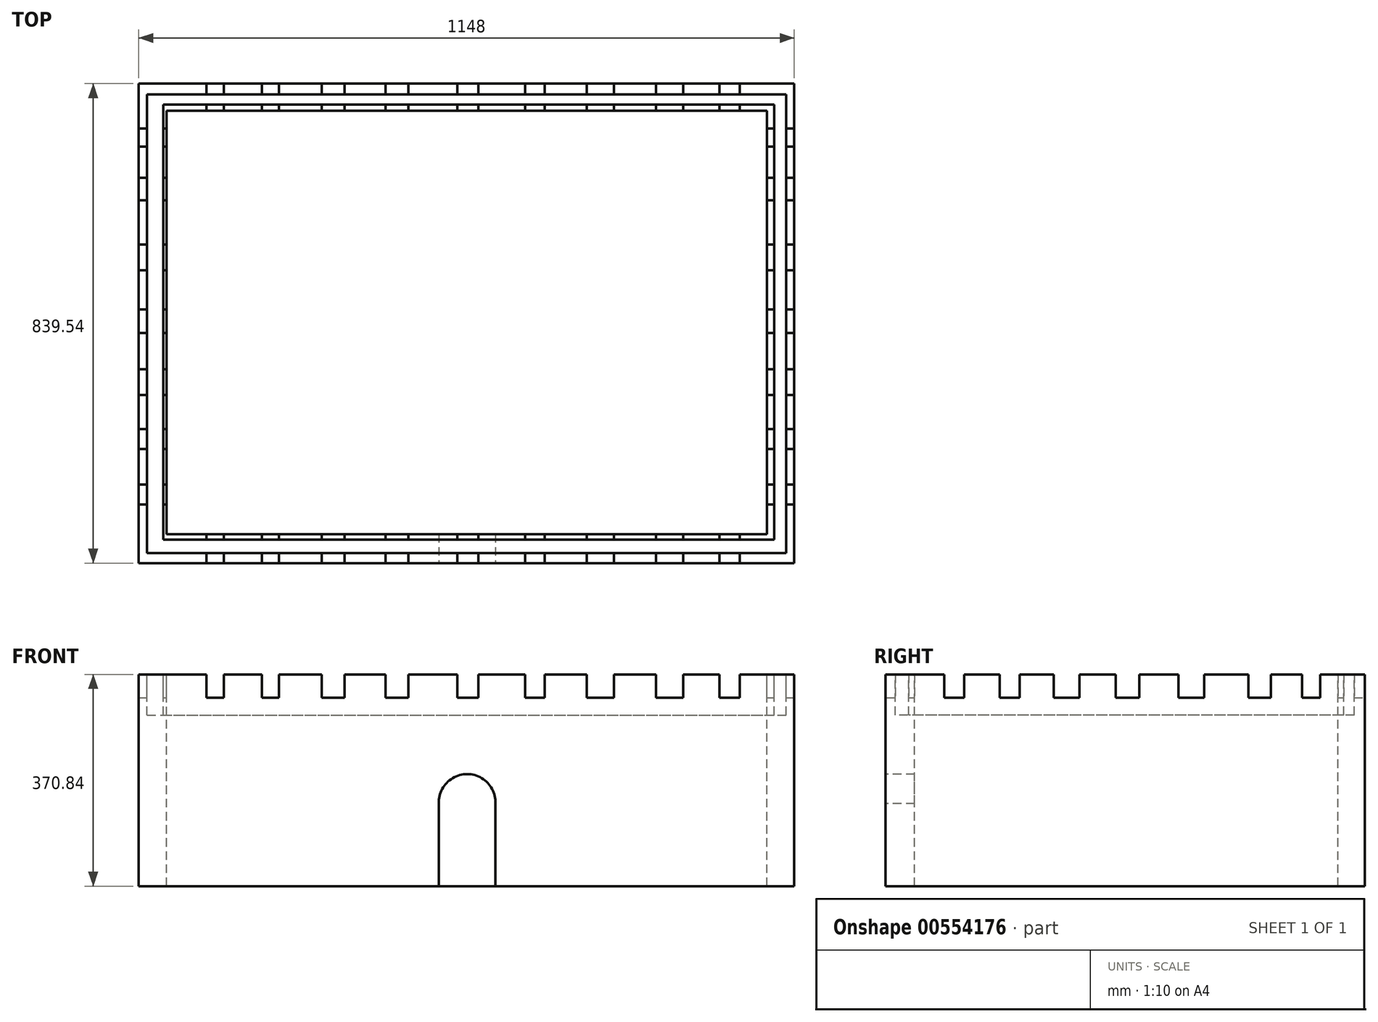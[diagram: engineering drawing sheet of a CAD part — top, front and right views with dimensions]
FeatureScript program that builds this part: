
annotation { "Feature Type Name" : "Feature", "Feature Type Description" : "" }
export const myFeature = defineFeature(function(context is Context, id is Id, definition is map)
    precondition{}
    {
        {
            var Q0;
            Q0=qCreatedBy(makeId("Top.planeOp"),FACE);
            var sketch = newSketch(context, id + "F0", { "sketchPlane" : qUnion([Q0])});
            skLineSegment(sketch, "E0.bottom", {"start": v(-575.13, 417.36) * mm, "end": v(572.87, 417.36) * mm});
            skLineSegment(sketch, "E0.top", {"start": v(-575.13, -422.18) * mm, "end": v(572.87, -422.18) * mm});
            skLineSegment(sketch, "E0.left", {"start": v(-575.13, 417.36) * mm, "end": v(-575.13, -422.18) * mm});
            skLineSegment(sketch, "E0.right", {"start": v(572.87, 417.36) * mm, "end": v(572.87, -422.18) * mm});
            skSolve(sketch);
        }
        {
            var Q0;
            Q0=makeQuery(id+"F0.imprint","IMPRINT",FACE,{"disambiguationData":[TD([[makeQuery(id+"F0.imprint","IMPRINT",EDGE,{"derivedFrom":sQuery(id+"F0.wireOp",EDGE,"E0.bottom")}),-1.0]])]});
            extrude(context, id + "F1", {"entities" : qUnion([Q0]), "depth" : 370.84 * mm, "offsetDistance" : 25.4 * mm});
        }
        {
            var Q0;
            Q0=makeQuery(id+"F1.opExtrude","CAP_FACE",FACE,{"disambiguationData":[OSD([sQuery(id+"F0.wireOp",EDGE,"E0.bottom"),sQuery(id+"F0.wireOp",EDGE,"E0.top"),sQuery(id+"F0.wireOp",EDGE,"E0.left"),sQuery(id+"F0.wireOp",EDGE,"E0.right")])],"isStart":false});
            var sketch = newSketch(context, id + "F2", { "sketchPlane" : qUnion([Q0])});
            skLineSegment(sketch, "E1.bottom", {"start": v(-523.99, 369.8) * mm, "end": v(524.91, 369.8) * mm});
            skLineSegment(sketch, "E1.top", {"start": v(-523.99, -369.85) * mm, "end": v(524.91, -369.85) * mm});
            skLineSegment(sketch, "E1.left", {"start": v(-523.99, 369.8) * mm, "end": v(-523.99, -369.85) * mm});
            skLineSegment(sketch, "E1.right", {"start": v(524.91, 369.8) * mm, "end": v(524.91, -369.85) * mm});
            skSolve(sketch);
        }
        {
            var Q0;
            Q0=makeQuery(id+"F1.opExtrude","CAP_FACE",FACE,{"disambiguationData":[OSD([sQuery(id+"F0.wireOp",EDGE,"E0.bottom"),sQuery(id+"F0.wireOp",EDGE,"E0.top"),sQuery(id+"F0.wireOp",EDGE,"E0.left"),sQuery(id+"F0.wireOp",EDGE,"E0.right")])],"isStart":false});
            var sketch = newSketch(context, id + "F3", { "sketchPlane" : qUnion([Q0])});
            skSolve(sketch);
        }
        {
            var Q0;
            Q0 = qSketchRegion(id + "F2", true);
            extrude(context, id + "F4", {"entities" : qUnion([Q0]), "operationType" : NewBodyOperationType.REMOVE, "oppositeDirection" : true, "depth" : 386.08 * mm, "offsetDistance" : 25.4 * mm});
        }
        {
            var Q0;
            Q0=makeQuery(id+"F3.imprint","IMPRINT",FACE,{"disambiguationData":[TD([[makeQuery(id+"F3.imprint","IMPRINT",EDGE,{"derivedFrom":makeQuery(id+"F1.opExtrude","CAP_EDGE",EDGE,{"disambiguationData":[OSD([sQuery(id+"F0.wireOp",EDGE,"E0.bottom")])],"isStart":false})}),-1.0]])]});
            var sketch = newSketch(context, id + "F5", { "sketchPlane" : qUnion([Q0])});
            skLineSegment(sketch, "E2.bottom", {"start": v(-560.65, 398.5) * mm, "end": v(558.39, 398.5) * mm});
            skLineSegment(sketch, "E2.top", {"start": v(-560.65, -404.92) * mm, "end": v(558.39, -404.92) * mm});
            skLineSegment(sketch, "E2.left", {"start": v(-560.65, 398.5) * mm, "end": v(-560.65, -404.92) * mm});
            skLineSegment(sketch, "E2.right", {"start": v(558.39, 398.5) * mm, "end": v(558.39, -404.92) * mm});
            skSolve(sketch);
        }
        {
            var Q0;
            Q0 = qSketchRegion(id + "F5", true);
            extrude(context, id + "F6", {"entities" : qUnion([Q0]), "operationType" : NewBodyOperationType.REMOVE, "oppositeDirection" : true, "depth" : 71.12 * mm, "offsetDistance" : 25.4 * mm});
        }
        {
            var Q0;
            Q0=makeQuery(id+"F3.imprint","IMPRINT",FACE,{"disambiguationData":[TD([[makeQuery(id+"F3.imprint","IMPRINT",EDGE,{"derivedFrom":makeQuery(id+"F1.opExtrude","CAP_EDGE",EDGE,{"disambiguationData":[OSD([sQuery(id+"F0.wireOp",EDGE,"E0.bottom")])],"isStart":false})}),-1.0]])]});
            var sketch = newSketch(context, id + "F7", { "sketchPlane" : qUnion([Q0])});
            skLineSegment(sketch, "E3.bottom", {"start": v(-532.12, 380.5) * mm, "end": v(537.5, 380.5) * mm});
            skLineSegment(sketch, "E3.top", {"start": v(-532.12, -381.47) * mm, "end": v(537.5, -381.47) * mm});
            skLineSegment(sketch, "E3.left", {"start": v(-532.12, 380.5) * mm, "end": v(-532.12, -381.47) * mm});
            skLineSegment(sketch, "E3.right", {"start": v(537.5, 380.5) * mm, "end": v(537.5, -381.47) * mm});
            skSolve(sketch);
        }
        {
            var Q0;
            Q0 = qSketchRegion(id + "F7", true);
            extrude(context, id + "F8", {"entities" : qUnion([Q0]), "operationType" : NewBodyOperationType.ADD, "oppositeDirection" : true, "depth" : 271.78 * mm, "offsetDistance" : 25.4 * mm});
        }
        {
            var Q0;
            Q0=makeQuery(id+"F3.imprint","IMPRINT",FACE,{"disambiguationData":[TD([[makeQuery(id+"F3.imprint","IMPRINT",EDGE,{"derivedFrom":makeQuery(id+"F1.opExtrude","CAP_EDGE",EDGE,{"disambiguationData":[OSD([sQuery(id+"F0.wireOp",EDGE,"E0.bottom")])],"isStart":false})}),-1.0]])]});
            var sketch = newSketch(context, id + "F9", { "sketchPlane" : qUnion([Q0])});
            skLineSegment(sketch, "E4.bottom", {"start": v(-526.8, 369.85) * mm, "end": v(524.91, 369.85) * mm});
            skLineSegment(sketch, "E4.top", {"start": v(-526.8, -371.46) * mm, "end": v(524.91, -371.46) * mm});
            skLineSegment(sketch, "E4.left", {"start": v(-526.8, 369.85) * mm, "end": v(-526.8, -371.46) * mm});
            skLineSegment(sketch, "E4.right", {"start": v(524.91, 369.85) * mm, "end": v(524.91, -371.46) * mm});
            skSolve(sketch);
        }
        {
            var Q0;
            Q0 = qSketchRegion(id + "F9", true);
            extrude(context, id + "F10", {"entities" : qUnion([Q0]), "operationType" : NewBodyOperationType.REMOVE, "oppositeDirection" : true, "depth" : 421.64 * mm, "offsetDistance" : 25.4 * mm});
        }
        {
            var Q0;
            Q0=makeQuery(id+"F3.imprint","IMPRINT",FACE,{"disambiguationData":[TD([[makeQuery(id+"F3.imprint","IMPRINT",EDGE,{"derivedFrom":makeQuery(id+"F1.opExtrude","CAP_EDGE",EDGE,{"disambiguationData":[OSD([sQuery(id+"F0.wireOp",EDGE,"E0.bottom")])],"isStart":false})}),-1.0]])]});
            var sketch = newSketch(context, id + "F11", { "sketchPlane" : qUnion([Q0])});
            skLineSegment(sketch, "E5.bottom", {"start": v(-611.66, 22.3) * mm, "end": v(642.87, 22.3) * mm});
            skLineSegment(sketch, "E5.top", {"start": v(-611.66, -19.15) * mm, "end": v(642.87, -19.15) * mm});
            skLineSegment(sketch, "E5.left", {"start": v(-611.66, 22.3) * mm, "end": v(-611.66, -19.15) * mm});
            skLineSegment(sketch, "E5.right", {"start": v(642.87, 22.3) * mm, "end": v(642.87, -19.15) * mm});
            skLineSegment(sketch, "E6.bottom", {"start": v(153.5, 22.3) * mm, "end": v(153.5, 22.3) * mm});
            skLineSegment(sketch, "E6.top", {"start": v(153.5, -19.15) * mm, "end": v(153.5, -19.15) * mm});
            skLineSegment(sketch, "E6.left", {"start": v(153.5, 22.3) * mm, "end": v(153.5, -19.15) * mm});
            skLineSegment(sketch, "E6.right", {"start": v(153.5, 22.3) * mm, "end": v(153.5, -19.15) * mm});
            skSolve(sketch);
        }
        {
            var Q0;
            Q0 = qSketchRegion(id + "F11", true);
            extrude(context, id + "F12", {"entities" : qUnion([Q0]), "operationType" : NewBodyOperationType.REMOVE, "oppositeDirection" : true, "depth" : 40.64 * mm, "offsetDistance" : 25.4 * mm});
        }
        {
            var Q0;
            Q0=makeQuery(id+"F3.imprint","IMPRINT",FACE,{"disambiguationData":[TD([[makeQuery(id+"F3.imprint","IMPRINT",EDGE,{"derivedFrom":makeQuery(id+"F1.opExtrude","CAP_EDGE",EDGE,{"disambiguationData":[OSD([sQuery(id+"F0.wireOp",EDGE,"E0.bottom")])],"isStart":false})}),-1.0]])]});
            var sketch = newSketch(context, id + "F13", { "sketchPlane" : qUnion([Q0])});
            skLineSegment(sketch, "E7.bottom", {"start": v(-17.07, -430.42) * mm, "end": v(19.6, -430.42) * mm});
            skLineSegment(sketch, "E7.top", {"start": v(-17.07, 436.75) * mm, "end": v(19.6, 436.75) * mm});
            skLineSegment(sketch, "E7.left", {"start": v(-17.07, -430.42) * mm, "end": v(-17.07, 436.75) * mm});
            skLineSegment(sketch, "E7.right", {"start": v(19.6, -430.42) * mm, "end": v(19.6, 436.75) * mm});
            skSolve(sketch);
        }
        {
            var Q0;
            {var subQ0=sQuery(id+"F13.wireOp",EDGE,"E7.left");var subQ1=makeQuery(id+"F3.imprint","IMPRINT",EDGE,{"derivedFrom":makeQuery(id+"F1.opExtrude","CAP_EDGE",EDGE,{"disambiguationData":[OSD([sQuery(id+"F0.wireOp",EDGE,"E0.top")])],"isStart":false})});var subQ2=makeQuery(id+"F13.imprint","INTERSECT",VERTEX,{"derivedFrom":[subQ1,subQ0]});Q0=makeQuery(id+"F13.imprint","IMPRINT",FACE,{"disambiguationData":[TD([[makeQuery(id+"F13.imprint","IMPRINT",EDGE,{"disambiguationData":[TD([[subQ2,-1.0]])],"derivedFrom":subQ0}),-1.0]])]});}
            extrude(context, id + "F14", {"entities" : qUnion([Q0]), "operationType" : NewBodyOperationType.REMOVE, "oppositeDirection" : true, "depth" : 40.64 * mm, "offsetDistance" : 25.4 * mm});
        }
        {
            var Q0;
            Q0=makeQuery(id+"F3.imprint","IMPRINT",FACE,{"disambiguationData":[TD([[makeQuery(id+"F3.imprint","IMPRINT",EDGE,{"derivedFrom":makeQuery(id+"F1.opExtrude","CAP_EDGE",EDGE,{"disambiguationData":[OSD([sQuery(id+"F0.wireOp",EDGE,"E0.bottom")])],"isStart":false})}),-1.0]])]});
            var sketch = newSketch(context, id + "F15", { "sketchPlane" : qUnion([Q0])});
            skLineSegment(sketch, "E8.bottom", {"start": v(-103.15, 424) * mm, "end": v(-143, 424) * mm});
            skLineSegment(sketch, "E8.top", {"start": v(-103.15, -433.6) * mm, "end": v(-143, -433.6) * mm});
            skLineSegment(sketch, "E8.left", {"start": v(-103.15, 424) * mm, "end": v(-103.15, -433.6) * mm});
            skLineSegment(sketch, "E8.right", {"start": v(-143, 424) * mm, "end": v(-143, -433.6) * mm});
            skSolve(sketch);
        }
        {
            var Q0;
            Q0 = qSketchRegion(id + "F15", true);
            extrude(context, id + "F16", {"entities" : qUnion([Q0]), "operationType" : NewBodyOperationType.REMOVE, "oppositeDirection" : true, "depth" : 40.64 * mm, "offsetDistance" : 25.4 * mm});
        }
        {
            var Q0;
            Q0=makeQuery(id+"F3.imprint","IMPRINT",FACE,{"disambiguationData":[TD([[makeQuery(id+"F3.imprint","IMPRINT",EDGE,{"derivedFrom":makeQuery(id+"F1.opExtrude","CAP_EDGE",EDGE,{"disambiguationData":[OSD([sQuery(id+"F0.wireOp",EDGE,"E0.bottom")])],"isStart":false})}),-1.0]])]});
            var sketch = newSketch(context, id + "F17", { "sketchPlane" : qUnion([Q0])});
            skLineSegment(sketch, "E9.bottom", {"start": v(101.33, 424.13) * mm, "end": v(135.45, 424.13) * mm});
            skLineSegment(sketch, "E9.top", {"start": v(101.33, -425.13) * mm, "end": v(135.45, -425.13) * mm});
            skLineSegment(sketch, "E9.left", {"start": v(101.33, 424.13) * mm, "end": v(101.33, -425.13) * mm});
            skLineSegment(sketch, "E9.right", {"start": v(135.45, 424.13) * mm, "end": v(135.45, -425.13) * mm});
            skSolve(sketch);
        }
        {
            var Q0;
            Q0 = qSketchRegion(id + "F17", true);
            extrude(context, id + "F18", {"entities" : qUnion([Q0]), "operationType" : NewBodyOperationType.REMOVE, "oppositeDirection" : true, "depth" : 40.64 * mm, "offsetDistance" : 25.4 * mm});
        }
        {
            var Q0;
            Q0=makeQuery(id+"F3.imprint","IMPRINT",FACE,{"disambiguationData":[TD([[makeQuery(id+"F3.imprint","IMPRINT",EDGE,{"derivedFrom":makeQuery(id+"F1.opExtrude","CAP_EDGE",EDGE,{"disambiguationData":[OSD([sQuery(id+"F0.wireOp",EDGE,"E0.bottom")])],"isStart":false})}),-1.0]])]});
            var sketch = newSketch(context, id + "F19", { "sketchPlane" : qUnion([Q0])});
            skLineSegment(sketch, "E10.bottom", {"start": v(-214.74, 427.19) * mm, "end": v(-254.59, 427.19) * mm});
            skLineSegment(sketch, "E10.top", {"start": v(-214.74, -433.6) * mm, "end": v(-254.59, -433.6) * mm});
            skLineSegment(sketch, "E10.left", {"start": v(-214.74, 427.19) * mm, "end": v(-214.74, -433.6) * mm});
            skLineSegment(sketch, "E10.right", {"start": v(-254.59, 427.19) * mm, "end": v(-254.59, -433.6) * mm});
            skSolve(sketch);
        }
        {
            var Q0;
            Q0 = qSketchRegion(id + "F19", true);
            extrude(context, id + "F20", {"entities" : qUnion([Q0]), "operationType" : NewBodyOperationType.REMOVE, "oppositeDirection" : true, "depth" : 40.64 * mm, "offsetDistance" : 25.4 * mm});
        }
        {
            var Q0;
            Q0=makeQuery(id+"F3.imprint","IMPRINT",FACE,{"disambiguationData":[TD([[makeQuery(id+"F3.imprint","IMPRINT",EDGE,{"derivedFrom":makeQuery(id+"F1.opExtrude","CAP_EDGE",EDGE,{"disambiguationData":[OSD([sQuery(id+"F0.wireOp",EDGE,"E0.bottom")])],"isStart":false})}),-1.0]])]});
            var sketch = newSketch(context, id + "F21", { "sketchPlane" : qUnion([Q0])});
            skLineSegment(sketch, "E11.bottom", {"start": v(-329.55, 425.56) * mm, "end": v(-359.86, 425.56) * mm});
            skLineSegment(sketch, "E11.top", {"start": v(-329.55, -459.36) * mm, "end": v(-359.86, -459.36) * mm});
            skLineSegment(sketch, "E11.left", {"start": v(-329.55, 425.56) * mm, "end": v(-329.55, -459.36) * mm});
            skLineSegment(sketch, "E11.right", {"start": v(-359.86, 425.56) * mm, "end": v(-359.86, -459.36) * mm});
            skSolve(sketch);
        }
        {
            var Q0;
            Q0 = qSketchRegion(id + "F21", true);
            extrude(context, id + "F22", {"entities" : qUnion([Q0]), "operationType" : NewBodyOperationType.REMOVE, "oppositeDirection" : true, "depth" : 40.64 * mm, "offsetDistance" : 25.4 * mm});
        }
        {
            var Q0;
            Q0=makeQuery(id+"F3.imprint","IMPRINT",FACE,{"disambiguationData":[TD([[makeQuery(id+"F3.imprint","IMPRINT",EDGE,{"derivedFrom":makeQuery(id+"F1.opExtrude","CAP_EDGE",EDGE,{"disambiguationData":[OSD([sQuery(id+"F0.wireOp",EDGE,"E0.bottom")])],"isStart":false})}),-1.0]])]});
            var sketch = newSketch(context, id + "F23", { "sketchPlane" : qUnion([Q0])});
            skLineSegment(sketch, "E12.bottom", {"start": v(-426.3, 422.82) * mm, "end": v(-456.6, 422.82) * mm});
            skLineSegment(sketch, "E12.top", {"start": v(-426.3, -426.82) * mm, "end": v(-456.6, -426.82) * mm});
            skLineSegment(sketch, "E12.left", {"start": v(-426.3, 422.82) * mm, "end": v(-426.3, -426.82) * mm});
            skLineSegment(sketch, "E12.right", {"start": v(-456.6, 422.82) * mm, "end": v(-456.6, -426.82) * mm});
            skSolve(sketch);
        }
        {
            var Q0;
            Q0 = qSketchRegion(id + "F23", true);
            extrude(context, id + "F24", {"entities" : qUnion([Q0]), "operationType" : NewBodyOperationType.REMOVE, "oppositeDirection" : true, "depth" : 40.64 * mm, "offsetDistance" : 25.4 * mm});
        }
        {
            var Q0;
            Q0=makeQuery(id+"F3.imprint","IMPRINT",FACE,{"disambiguationData":[TD([[makeQuery(id+"F3.imprint","IMPRINT",EDGE,{"derivedFrom":makeQuery(id+"F1.opExtrude","CAP_EDGE",EDGE,{"disambiguationData":[OSD([sQuery(id+"F0.wireOp",EDGE,"E0.bottom")])],"isStart":false})}),-1.0]])]});
            var sketch = newSketch(context, id + "F25", { "sketchPlane" : qUnion([Q0])});
            skLineSegment(sketch, "E13.bottom", {"start": v(209.29, 427.19) * mm, "end": v(257.1, 427.19) * mm});
            skLineSegment(sketch, "E13.top", {"start": v(209.29, -432.01) * mm, "end": v(257.1, -432.01) * mm});
            skLineSegment(sketch, "E13.left", {"start": v(209.29, 427.19) * mm, "end": v(209.29, -432.01) * mm});
            skLineSegment(sketch, "E13.right", {"start": v(257.1, 427.19) * mm, "end": v(257.1, -432.01) * mm});
            skSolve(sketch);
        }
        {
            var Q0;
            Q0 = qSketchRegion(id + "F25", true);
            extrude(context, id + "F26", {"entities" : qUnion([Q0]), "operationType" : NewBodyOperationType.REMOVE, "oppositeDirection" : true, "depth" : 40.64 * mm, "offsetDistance" : 25.4 * mm});
        }
        {
            var Q0;
            Q0=makeQuery(id+"F3.imprint","IMPRINT",FACE,{"disambiguationData":[TD([[makeQuery(id+"F3.imprint","IMPRINT",EDGE,{"derivedFrom":makeQuery(id+"F1.opExtrude","CAP_EDGE",EDGE,{"disambiguationData":[OSD([sQuery(id+"F0.wireOp",EDGE,"E0.bottom")])],"isStart":false})}),-1.0]])]});
            var sketch = newSketch(context, id + "F27", { "sketchPlane" : qUnion([Q0])});
            skLineSegment(sketch, "E14.bottom", {"start": v(330.44, 422.4) * mm, "end": v(378.26, 422.4) * mm});
            skLineSegment(sketch, "E14.top", {"start": v(330.44, -436.8) * mm, "end": v(378.26, -436.8) * mm});
            skLineSegment(sketch, "E14.left", {"start": v(330.44, 422.4) * mm, "end": v(330.44, -436.8) * mm});
            skLineSegment(sketch, "E14.right", {"start": v(378.26, 422.4) * mm, "end": v(378.26, -436.8) * mm});
            skSolve(sketch);
        }
        {
            var Q0;
            Q0 = qSketchRegion(id + "F27", true);
            extrude(context, id + "F28", {"entities" : qUnion([Q0]), "operationType" : NewBodyOperationType.REMOVE, "oppositeDirection" : true, "depth" : 40.64 * mm, "offsetDistance" : 25.4 * mm});
        }
        {
            var Q0;
            Q0=makeQuery(id+"F3.imprint","IMPRINT",FACE,{"disambiguationData":[TD([[makeQuery(id+"F3.imprint","IMPRINT",EDGE,{"derivedFrom":makeQuery(id+"F1.opExtrude","CAP_EDGE",EDGE,{"disambiguationData":[OSD([sQuery(id+"F0.wireOp",EDGE,"E0.bottom")])],"isStart":false})}),-1.0]])]});
            var sketch = newSketch(context, id + "F29", { "sketchPlane" : qUnion([Q0])});
            skLineSegment(sketch, "E15.bottom", {"start": v(442.02, 427.19) * mm, "end": v(477.1, 427.19) * mm});
            skLineSegment(sketch, "E15.top", {"start": v(442.02, -438.4) * mm, "end": v(477.1, -438.4) * mm});
            skLineSegment(sketch, "E15.left", {"start": v(442.02, 427.19) * mm, "end": v(442.02, -438.4) * mm});
            skLineSegment(sketch, "E15.right", {"start": v(477.1, 427.19) * mm, "end": v(477.1, -438.4) * mm});
            skSolve(sketch);
        }
        {
            var Q0;
            Q0 = qSketchRegion(id + "F29", true);
            extrude(context, id + "F30", {"entities" : qUnion([Q0]), "operationType" : NewBodyOperationType.REMOVE, "oppositeDirection" : true, "depth" : 40.64 * mm, "offsetDistance" : 25.4 * mm});
        }
        {
            var Q0;
            Q0=makeQuery(id+"F3.imprint","IMPRINT",FACE,{"disambiguationData":[TD([[makeQuery(id+"F3.imprint","IMPRINT",EDGE,{"derivedFrom":makeQuery(id+"F1.opExtrude","CAP_EDGE",EDGE,{"disambiguationData":[OSD([sQuery(id+"F0.wireOp",EDGE,"E0.bottom")])],"isStart":false})}),-1.0]])]});
            var sketch = newSketch(context, id + "F31", { "sketchPlane" : qUnion([Q0])});
            skLineSegment(sketch, "E16.bottom", {"start": v(-587.75, 90.84) * mm, "end": v(598.24, 90.84) * mm});
            skLineSegment(sketch, "E16.top", {"start": v(-587.75, 135.47) * mm, "end": v(598.24, 135.47) * mm});
            skLineSegment(sketch, "E16.left", {"start": v(-587.75, 90.84) * mm, "end": v(-587.75, 135.47) * mm});
            skLineSegment(sketch, "E16.right", {"start": v(598.24, 90.84) * mm, "end": v(598.24, 135.47) * mm});
            skSolve(sketch);
        }
        {
            var Q0;
            Q0 = qSketchRegion(id + "F31", true);
            extrude(context, id + "F32", {"entities" : qUnion([Q0]), "operationType" : NewBodyOperationType.REMOVE, "oppositeDirection" : true, "depth" : 40.64 * mm, "offsetDistance" : 25.4 * mm});
        }
        {
            var Q0;
            Q0=makeQuery(id+"F3.imprint","IMPRINT",FACE,{"disambiguationData":[TD([[makeQuery(id+"F3.imprint","IMPRINT",EDGE,{"derivedFrom":makeQuery(id+"F1.opExtrude","CAP_EDGE",EDGE,{"disambiguationData":[OSD([sQuery(id+"F0.wireOp",EDGE,"E0.bottom")])],"isStart":false})}),-1.0]])]});
            var sketch = newSketch(context, id + "F33", { "sketchPlane" : qUnion([Q0])});
            skLineSegment(sketch, "E17.bottom", {"start": v(-584.56, -82.91) * mm, "end": v(591.86, -82.91) * mm});
            skLineSegment(sketch, "E17.top", {"start": v(-584.56, -127.55) * mm, "end": v(591.86, -127.55) * mm});
            skLineSegment(sketch, "E17.left", {"start": v(-584.56, -82.91) * mm, "end": v(-584.56, -127.55) * mm});
            skLineSegment(sketch, "E17.right", {"start": v(591.86, -82.91) * mm, "end": v(591.86, -127.55) * mm});
            skSolve(sketch);
        }
        {
            var Q0;
            Q0 = qSketchRegion(id + "F33", true);
            extrude(context, id + "F34", {"entities" : qUnion([Q0]), "operationType" : NewBodyOperationType.REMOVE, "oppositeDirection" : true, "depth" : 40.64 * mm, "offsetDistance" : 25.4 * mm});
        }
        {
            var Q0;
            Q0=makeQuery(id+"F3.imprint","IMPRINT",FACE,{"disambiguationData":[TD([[makeQuery(id+"F3.imprint","IMPRINT",EDGE,{"derivedFrom":makeQuery(id+"F1.opExtrude","CAP_EDGE",EDGE,{"disambiguationData":[OSD([sQuery(id+"F0.wireOp",EDGE,"E0.bottom")])],"isStart":false})}),-1.0]])]});
            var sketch = newSketch(context, id + "F35", { "sketchPlane" : qUnion([Q0])});
            skLineSegment(sketch, "E18.bottom", {"start": v(591.66, 213) * mm, "end": v(-608.3, 213) * mm});
            skLineSegment(sketch, "E18.top", {"start": v(591.66, 252.8) * mm, "end": v(-608.3, 252.8) * mm});
            skLineSegment(sketch, "E18.left", {"start": v(591.66, 213) * mm, "end": v(591.66, 252.8) * mm});
            skLineSegment(sketch, "E18.right", {"start": v(-608.3, 213) * mm, "end": v(-608.3, 252.8) * mm});
            skSolve(sketch);
        }
        {
            var Q0;
            Q0 = qSketchRegion(id + "F35", true);
            extrude(context, id + "F36", {"entities" : qUnion([Q0]), "operationType" : NewBodyOperationType.REMOVE, "oppositeDirection" : true, "depth" : 40.64 * mm, "offsetDistance" : 25.4 * mm});
        }
        {
            var Q0;
            Q0=makeQuery(id+"F3.imprint","IMPRINT",FACE,{"disambiguationData":[TD([[makeQuery(id+"F3.imprint","IMPRINT",EDGE,{"derivedFrom":makeQuery(id+"F1.opExtrude","CAP_EDGE",EDGE,{"disambiguationData":[OSD([sQuery(id+"F0.wireOp",EDGE,"E0.bottom")])],"isStart":false})}),-1.0]])]});
            var sketch = newSketch(context, id + "F37", { "sketchPlane" : qUnion([Q0])});
            skLineSegment(sketch, "E19.bottom", {"start": v(587, 306.96) * mm, "end": v(-610.15, 306.96) * mm});
            skLineSegment(sketch, "E19.top", {"start": v(587, 338.84) * mm, "end": v(-610.15, 338.84) * mm});
            skLineSegment(sketch, "E19.left", {"start": v(587, 306.96) * mm, "end": v(587, 338.84) * mm});
            skLineSegment(sketch, "E19.right", {"start": v(-610.15, 306.96) * mm, "end": v(-610.15, 338.84) * mm});
            skSolve(sketch);
        }
        {
            var Q0;
            Q0 = qSketchRegion(id + "F37", true);
            extrude(context, id + "F38", {"entities" : qUnion([Q0]), "operationType" : NewBodyOperationType.REMOVE, "oppositeDirection" : true, "depth" : 40.64 * mm, "offsetDistance" : 25.4 * mm});
        }
        {
            var Q0;
            Q0=makeQuery(id+"F3.imprint","IMPRINT",FACE,{"disambiguationData":[TD([[makeQuery(id+"F3.imprint","IMPRINT",EDGE,{"derivedFrom":makeQuery(id+"F1.opExtrude","CAP_EDGE",EDGE,{"disambiguationData":[OSD([sQuery(id+"F0.wireOp",EDGE,"E0.bottom")])],"isStart":false})}),-1.0]])]});
            var sketch = newSketch(context, id + "F39", { "sketchPlane" : qUnion([Q0])});
            skLineSegment(sketch, "E20.bottom", {"start": v(-581.93, -187.69) * mm, "end": v(588.28, -187.69) * mm});
            skLineSegment(sketch, "E20.top", {"start": v(-581.93, -222.54) * mm, "end": v(588.28, -222.54) * mm});
            skLineSegment(sketch, "E20.left", {"start": v(-581.93, -187.69) * mm, "end": v(-581.93, -222.54) * mm});
            skLineSegment(sketch, "E20.right", {"start": v(588.28, -187.69) * mm, "end": v(588.28, -222.54) * mm});
            skSolve(sketch);
        }
        {
            var Q0;
            Q0 = qSketchRegion(id + "F39", true);
            extrude(context, id + "F40", {"entities" : qUnion([Q0]), "operationType" : NewBodyOperationType.REMOVE, "oppositeDirection" : true, "depth" : 40.64 * mm, "offsetDistance" : 25.4 * mm});
        }
        {
            var Q0;
            Q0=makeQuery(id+"F3.imprint","IMPRINT",FACE,{"disambiguationData":[TD([[makeQuery(id+"F3.imprint","IMPRINT",EDGE,{"derivedFrom":makeQuery(id+"F1.opExtrude","CAP_EDGE",EDGE,{"disambiguationData":[OSD([sQuery(id+"F0.wireOp",EDGE,"E0.bottom")])],"isStart":false})}),-1.0]])]});
            var sketch = newSketch(context, id + "F41", { "sketchPlane" : qUnion([Q0])});
            skLineSegment(sketch, "E21.bottom", {"start": v(-587.4, -284.86) * mm, "end": v(585.5, -284.86) * mm});
            skLineSegment(sketch, "E21.top", {"start": v(-587.4, -319.7) * mm, "end": v(585.5, -319.7) * mm});
            skLineSegment(sketch, "E21.left", {"start": v(-587.4, -284.86) * mm, "end": v(-587.4, -319.7) * mm});
            skLineSegment(sketch, "E21.right", {"start": v(585.5, -284.86) * mm, "end": v(585.5, -319.7) * mm});
            skSolve(sketch);
        }
        {
            var Q0;
            Q0 = qSketchRegion(id + "F41", true);
            extrude(context, id + "F42", {"entities" : qUnion([Q0]), "operationType" : NewBodyOperationType.REMOVE, "oppositeDirection" : true, "depth" : 40.64 * mm, "offsetDistance" : 25.4 * mm});
        }
        {
            var Q0;
            Q0=makeQuery(id+"F1.opExtrude","SWEPT_FACE",FACE,{"disambiguationData":[OSD([sQuery(id+"F0.wireOp",EDGE,"E0.top")])]});
            var sketch = newSketch(context, id + "F43", { "sketchPlane" : qUnion([Q0])});
            skCircle(sketch, "E22", {"center": v(0, 146.45) * mm, "radius": 49.69 * mm});
            skSolve(sketch);
        }
        {
            var Q0;
            Q0 = qSketchRegion(id + "F43", true);
            extrude(context, id + "F44", {"entities" : qUnion([Q0]), "operationType" : NewBodyOperationType.REMOVE, "oppositeDirection" : true, "depth" : 93.98 * mm, "offsetDistance" : 25.4 * mm});
        }
        {
            var Q0;
            Q0=makeQuery(id+"F1.opExtrude","SWEPT_FACE",FACE,{"disambiguationData":[OSD([sQuery(id+"F0.wireOp",EDGE,"E0.top")])]});
            var sketch = newSketch(context, id + "F45", { "sketchPlane" : qUnion([Q0])});
            skLineSegment(sketch, "E23.bottom", {"start": v(-49.97, 0) * mm, "end": v(49.65, 0) * mm});
            skLineSegment(sketch, "E23.top", {"start": v(-49.97, 144.43) * mm, "end": v(49.65, 144.43) * mm});
            skLineSegment(sketch, "E23.left", {"start": v(-49.97, 0) * mm, "end": v(-49.97, 144.43) * mm});
            skLineSegment(sketch, "E23.right", {"start": v(49.65, 0) * mm, "end": v(49.65, 144.43) * mm});
            skSolve(sketch);
        }
        {
            var Q0;
            Q0 = qSketchRegion(id + "F45", true);
            extrude(context, id + "F46", {"entities" : qUnion([Q0]), "operationType" : NewBodyOperationType.REMOVE, "oppositeDirection" : true, "depth" : 83.82 * mm, "offsetDistance" : 25.4 * mm});
        }
    });
